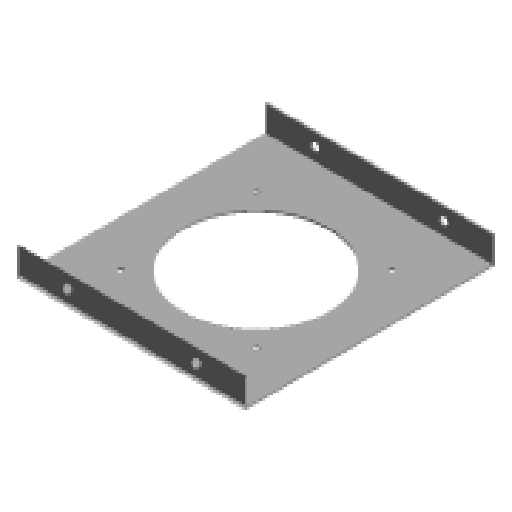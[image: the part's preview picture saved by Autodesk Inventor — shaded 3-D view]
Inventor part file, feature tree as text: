
AUTODESK INVENTOR PART (.ipt)
format: ipt  version: 2024 (Build 280153000, 153)  size: 148,992 bytes
history: native  units: mm
features: sketch x5, extrude x3, hole x2, delete_face x2
ambient origin geometry x8: Origin, YZ Plane, XZ Plane, XY Plane, X Axis, Y Axis, Z Axis, Center Point
bodies: Body1 (feature_tree)
feature tree (12):
  extrude  "Extrusion1"  Depth=177.0mm
  extrude  "Extrusion3"  Depth=1.5mm
  hole  "Bohrung1"  [1 undecoded]
  extrude  "Extrusion4"  Depth=177.0mm
  hole  "Bohrung2"  [1 undecoded]
  delete_face  "Delete Face1"
  delete_face  "Delete Face2"
  sketch  "Skizze1"  dims[d0=194.0mm d1=177.0mm]
  sketch  "Skizze4"  dims[d2=1.5mm d3=0.0mm d9=113.0mm]
  sketch  "Skizze5"  dims[d10=2.0mm d11=0.0mm d12=105.0mm]
  sketch  "Skizze8"  dims[d13=105.0mm]
  sketch  "Skizze9"  dims[d14=4.3mm d15=10.0mm d16=4.0mm d17=2.0mm d18=90.0deg d19=8.0mm d20=20.594885mm d32=177.0mm d33=1.5mm d34=177.0mm d35=1.5mm d36=20.0mm d37=0.0mm d40=100.0mm d42=177.0mm d43=10.0mm d44=10.0mm d45=6.1mm d46=6.0mm d47=4.0mm d48=2.0mm d49=90.0deg d50=8.0mm d51=20.594885mm d52=38.5mm]
note: 2 required parameter values undecoded (feature->parameter linkage not recoverable at this tier; creation-order binding heuristic only, values carry confidence <= 0.55)
